# Revit family: QF_BOURGEAT_Chariots_pour_transport_Assiettes_et_couverts
name_source: partatom
category: Equipement spécialisé
revit_build: Autodesk Revit 2015 (Build: 20140606_1530(x64)
units: mm (PartAtom-declared; Revit-internal decimal feet)

## types (8) — shared parameters
Barre renfort Longueur = 987 mm  [stored 3.23819 ft]
Certification = NF Alimentaire
Charge max = 200.00 kg
Fabricant = BOURGEAT
Longueur hors tout = 1112 mm  [stored 3.64829 ft]
Longueur support = 1032 mm
Spécification du Fabricant = Chariots à assiettes et couverts
URL catalogue = http://www.bourgeat.fr

## per-type parameters (varying)
| type | Barre de renfort | Barre renfort Largeur | Decal séparation bas | Hauteur echelle | Hauteur hors tout | Hauteur support | Hauteur séparation | Largeur séparation | Modèle | Profondeur echelle | Profondeur hors tout | Séparation standard | arceau petite vaisselle | arceau standard | decal support couverts | pare chute grand modele | pare chute petit modele |
| Chariot assiettes et couverts standard - Petit modèle | Non | 415 mm  [stored 1.36155 ft] | 138 mm | 627 mm  [stored 2.05709 ft] | 1014 mm  [stored 3.32677 ft] | 498 mm  [stored 1.63386 ft] | 531 mm  [stored 1.74213 ft] | 280 mm  [stored 0.918635 ft] | 792506 | 465 mm  [stored 1.52559 ft] | 540 mm  [stored 1.77165 ft] | Oui | Non | Oui | 118 mm | Non | Non |
| Chariot assiettes et couverts standard - Grand modèle | Non | 502 mm  [stored 1.64698 ft] | 197 mm | 627 mm  [stored 2.05709 ft] | 1014 mm  [stored 3.32677 ft] | 458 mm | 488 mm  [stored 1.60105 ft] | 435 mm  [stored 1.42717 ft] | 792806 | 552 mm  [stored 1.81102 ft] | 627 mm  [stored 2.05709 ft] | Oui | Non | Oui | 203 mm | Non | Non |
| Chariot assiettes et couverts réhaussé - Petit modèle | Oui | 415 mm  [stored 1.36155 ft] | 451 mm | 940 mm | 1327 mm  [stored 4.35367 ft] | 498 mm  [stored 1.63386 ft] | 531 mm  [stored 1.74213 ft] | 280 mm  [stored 0.918635 ft] | 792606 | 465 mm  [stored 1.52559 ft] | 540 mm  [stored 1.77165 ft] | Oui | Non | Oui | 118 mm | Non | Non |
| Chariot assiettes et couverts réhaussé - Grand modèle | Oui | 502 mm  [stored 1.64698 ft] | 510 mm | 940 mm | 1327 mm  [stored 4.35367 ft] | 458 mm | 488 mm  [stored 1.60105 ft] | 435 mm  [stored 1.42717 ft] | 792906 | 552 mm  [stored 1.81102 ft] | 627 mm  [stored 2.05709 ft] | Oui | Non | Oui | 203 mm | Non | Non |
| Chariot petite vaisselle et couverts réhaussé - Grand modèle | Oui | 502 mm  [stored 1.64698 ft] | 510 mm | 940 mm | 1327 mm  [stored 4.35367 ft] | 458 mm | 488 mm  [stored 1.60105 ft] | 435 mm  [stored 1.42717 ft] | 792906+792904 | 552 mm  [stored 1.81102 ft] | 627 mm  [stored 2.05709 ft] | Non | Oui | Non | 203 mm | Oui | Non |
| Chariot petite vaisselle et couverts réhaussé - Petit modèle | Oui | 415 mm  [stored 1.36155 ft] | 451 mm | 940 mm | 1327 mm  [stored 4.35367 ft] | 498 mm  [stored 1.63386 ft] | 531 mm  [stored 1.74213 ft] | 280 mm  [stored 0.918635 ft] | 792606+791904 | 465 mm  [stored 1.52559 ft] | 540 mm  [stored 1.77165 ft] | Non | Oui | Non | 118 mm | Non | Oui |
| Chariot petite vaisselle et couverts standard - Grand modèle | Non | 502 mm  [stored 1.64698 ft] | 197 mm | 627 mm  [stored 2.05709 ft] | 1014 mm  [stored 3.32677 ft] | 458 mm | 488 mm  [stored 1.60105 ft] | 435 mm  [stored 1.42717 ft] | 792806+792904 | 552 mm  [stored 1.81102 ft] | 627 mm  [stored 2.05709 ft] | Non | Oui | Non | 203 mm | Oui | Non |
| Chariot petite vaisselle et couverts standard - Petit modèle | Non | 415 mm  [stored 1.36155 ft] | 138 mm | 627 mm  [stored 2.05709 ft] | 1014 mm  [stored 3.32677 ft] | 498 mm  [stored 1.63386 ft] | 531 mm  [stored 1.74213 ft] | 280 mm  [stored 0.918635 ft] | 792506+791904 | 465 mm  [stored 1.52559 ft] | 540 mm  [stored 1.77165 ft] | Non | Oui | Non | 118 mm | Non | Oui |

note: [stored X ft] marks values corroborated as IEEE doubles in the binary element streams (Revit-internal decimal feet)

## geometry (parser evidence)
native form markers: Blend x8
no freeform markers — native parametric forms only
